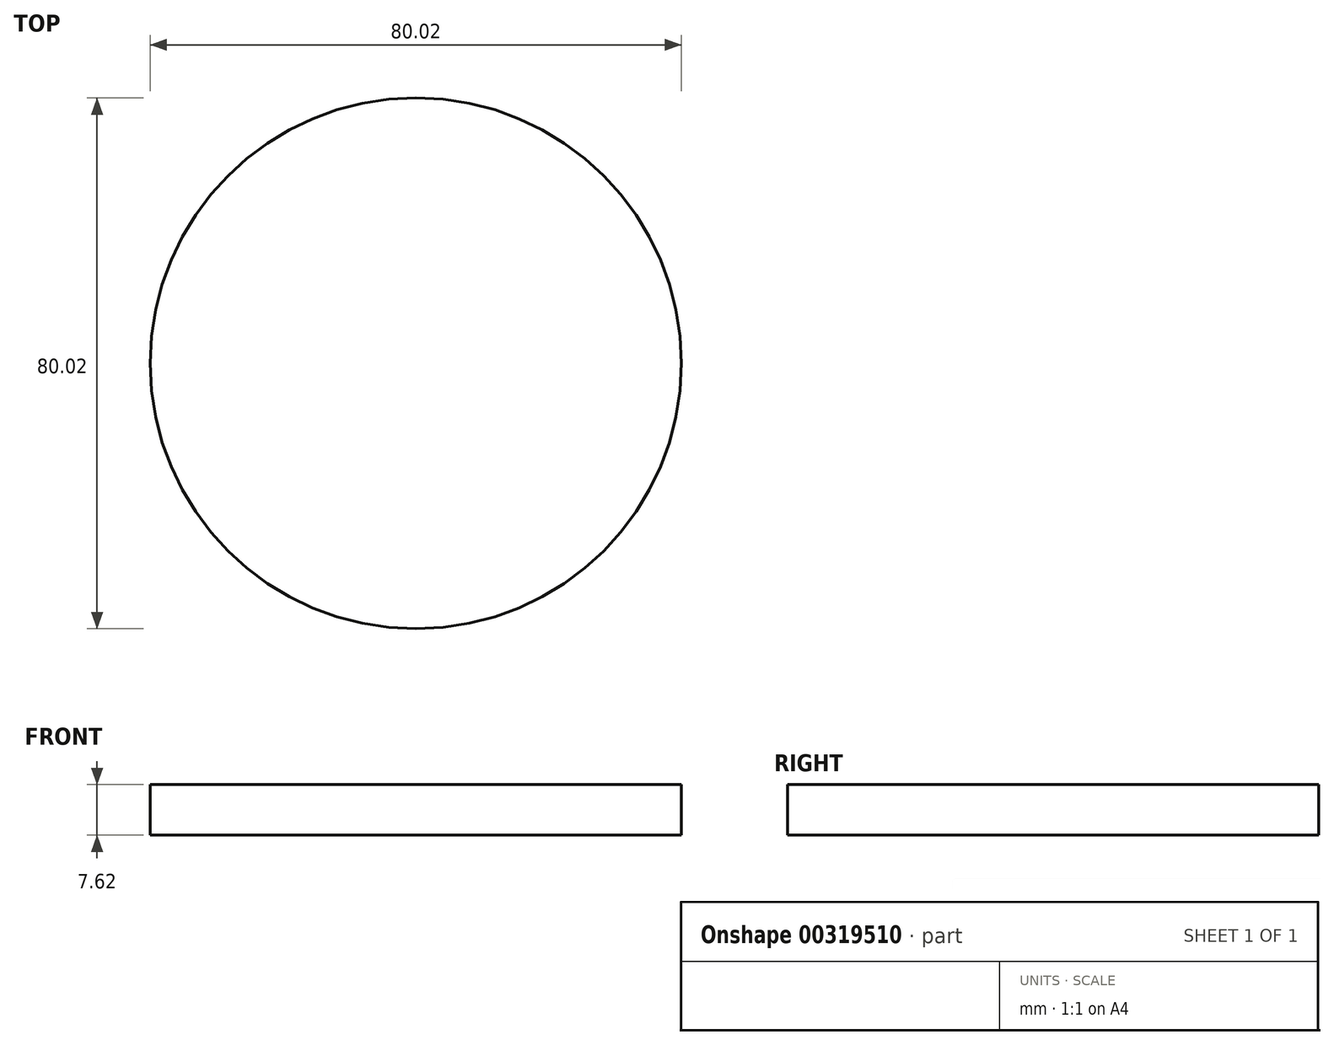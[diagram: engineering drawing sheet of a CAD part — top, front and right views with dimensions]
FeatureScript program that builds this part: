
annotation { "Feature Type Name" : "Feature", "Feature Type Description" : "" }
export const myFeature = defineFeature(function(context is Context, id is Id, definition is map)
    precondition{}
    {
        {
            var Q0;
            Q0=qCreatedBy(makeId("Top.planeOp"),FACE);
            var sketch = newSketch(context, id + "F0", { "sketchPlane" : qUnion([Q0])});
            skCircle(sketch, "E0", {"center": v(0, 0) * mm, "radius": 40 * mm});
            skSolve(sketch);
        }
        {
            var Q0;
            Q0 = qSketchRegion(id + "F0", true);
            extrude(context, id + "F1", {"entities" : qUnion([Q0]), "depth" : 7.62 * mm});
        }
    });
